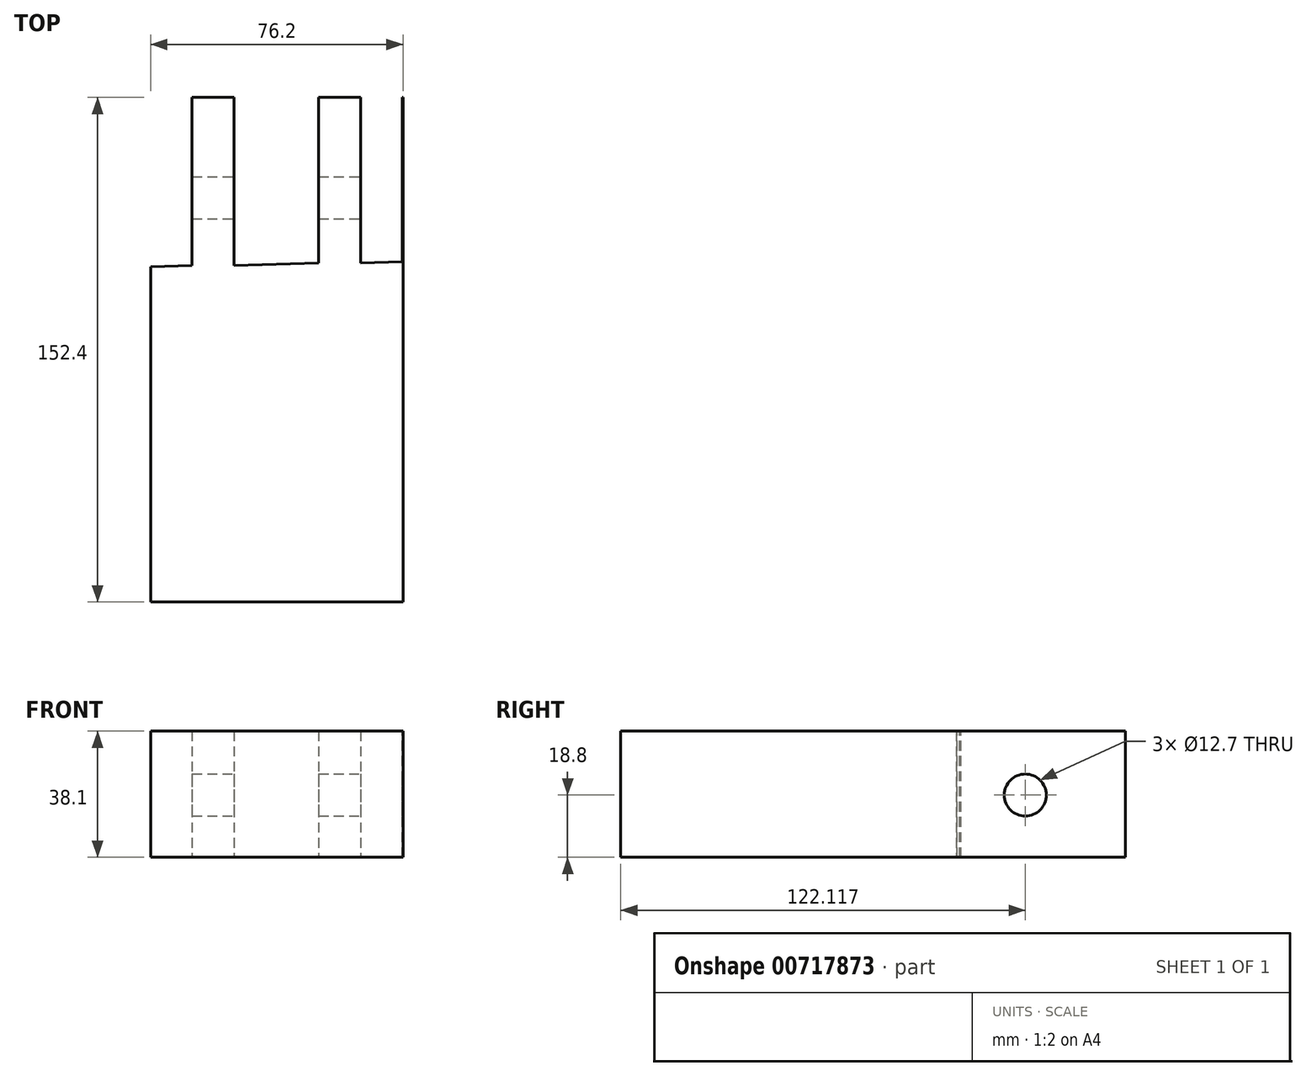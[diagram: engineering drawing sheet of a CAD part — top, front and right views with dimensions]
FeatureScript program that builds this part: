
annotation { "Feature Type Name" : "Feature", "Feature Type Description" : "" }
export const myFeature = defineFeature(function(context is Context, id is Id, definition is map)
    precondition{}
    {
        {
            var Q0;
            Q0=qCreatedBy(makeId("Front.planeOp"),FACE);
            var sketch = newSketch(context, id + "F0", { "sketchPlane" : qUnion([Q0])});
            skLineSegment(sketch, "E0", {"start": v(-217.78, 38.1) * mm, "end": v(-141.58, 38.1) * mm});
            skLineSegment(sketch, "E1", {"start": v(-141.58, 38.1) * mm, "end": v(-141.58, 0) * mm});
            skLineSegment(sketch, "E2", {"start": v(-141.58, 0) * mm, "end": v(-217.78, 0) * mm});
            skLineSegment(sketch, "E3", {"start": v(-217.78, 0) * mm, "end": v(-217.78, 38.1) * mm});
            skSolve(sketch);
        }
        {
            var Q0;
            Q0 = qSketchRegion(id + "F0", true);
            extrude(context, id + "F1", {"entities" : qUnion([Q0]), "endBound" : BoundingType.SYMMETRIC, "depth" : 152.4 * mm, "offsetDistance" : 25.4 * mm});
        }
        {
            var Q0;
            Q0=makeQuery(id+"F1.opExtrude","SWEPT_BODY",BODY,{"disambiguationData":[OSD([sQuery(id+"F0.wireOp",EDGE,"E0"),sQuery(id+"F0.wireOp",EDGE,"E1"),sQuery(id+"F0.wireOp",EDGE,"E2"),sQuery(id+"F0.wireOp",EDGE,"E3")])]});
            var Q1;
            Q1=qCreatedBy(makeId("Origin.pointOp"),VERTEX);
            transform(context, id + "F2", {"entities" : qUnion([Q0]), "transformType" : TransformType.TRANSLATION_3D, "dx" : 141.73 * mm, "dy" : 0 * mm, "dz" : -12.45 * mm, "makeCopy" : false});
        }
        {
            var Q0;
            Q0=qCreatedBy(makeId("Right.planeOp"),FACE);
            var sketch = newSketch(context, id + "F3", { "sketchPlane" : qUnion([Q0])});
            skCircle(sketch, "E4", {"center": v(45.92, 6.35) * mm, "radius": 6.35 * mm});
            skSolve(sketch);
        }
        {
            var Q0;
            Q0 = qSketchRegion(id + "F3", true);
            extrude(context, id + "F4", {"entities" : qUnion([Q0]), "operationType" : NewBodyOperationType.REMOVE, "endBound" : BoundingType.SYMMETRIC, "oppositeDirection" : true, "depth" : 170.7 * mm, "offsetDistance" : 25.4 * mm});
        }
        {
            var Q0;
            Q0=qCreatedBy(makeId("Top.planeOp"),FACE);
            var sketch = newSketch(context, id + "F5", { "sketchPlane" : qUnion([Q0])});
            skLineSegment(sketch, "E5", {"start": v(-63.5, 76.2) * mm, "end": v(-63.5, 25.4) * mm});
            skLineSegment(sketch, "E6", {"start": v(-50.8, 76.2) * mm, "end": v(-50.8, 25.4) * mm});
            skLineSegment(sketch, "E7", {"start": v(-12.61, 76.96) * mm, "end": v(-12.61, 26.16) * mm});
            skLineSegment(sketch, "E8", {"start": v(-25.31, 76.96) * mm, "end": v(-25.31, 26.16) * mm});
            skLineSegment(sketch, "E9", {"start": v(-50.8, 25.4) * mm, "end": v(-25.31, 26.16) * mm});
            skLineSegment(sketch, "E10", {"start": v(-50.8, 76.2) * mm, "end": v(-25.31, 76.96) * mm});
            skLineSegment(sketch, "E11", {"start": v(-63.5, 25.4) * mm, "end": v(-76.92, 25) * mm});
            skLineSegment(sketch, "E12", {"start": v(-76.92, 25) * mm, "end": v(-76.92, 76.96) * mm});
            skLineSegment(sketch, "E13", {"start": v(-76.92, 76.96) * mm, "end": v(-63.5, 76.2) * mm});
            skLineSegment(sketch, "E14", {"start": v(-12.61, 26.16) * mm, "end": v(0, 26.53) * mm});
            skLineSegment(sketch, "E15", {"start": v(0, 26.53) * mm, "end": v(0, 76.2) * mm});
            skLineSegment(sketch, "E16", {"start": v(0, 76.2) * mm, "end": v(-12.61, 76.96) * mm});
            skSolve(sketch);
        }
        {
            var Q0;
            Q0 = qSketchRegion(id + "F5", true);
            extrude(context, id + "F6", {"entities" : qUnion([Q0]), "operationType" : NewBodyOperationType.REMOVE, "endBound" : BoundingType.SYMMETRIC, "oppositeDirection" : true, "depth" : 101.6 * mm, "offsetDistance" : 25.4 * mm});
        }
    });
